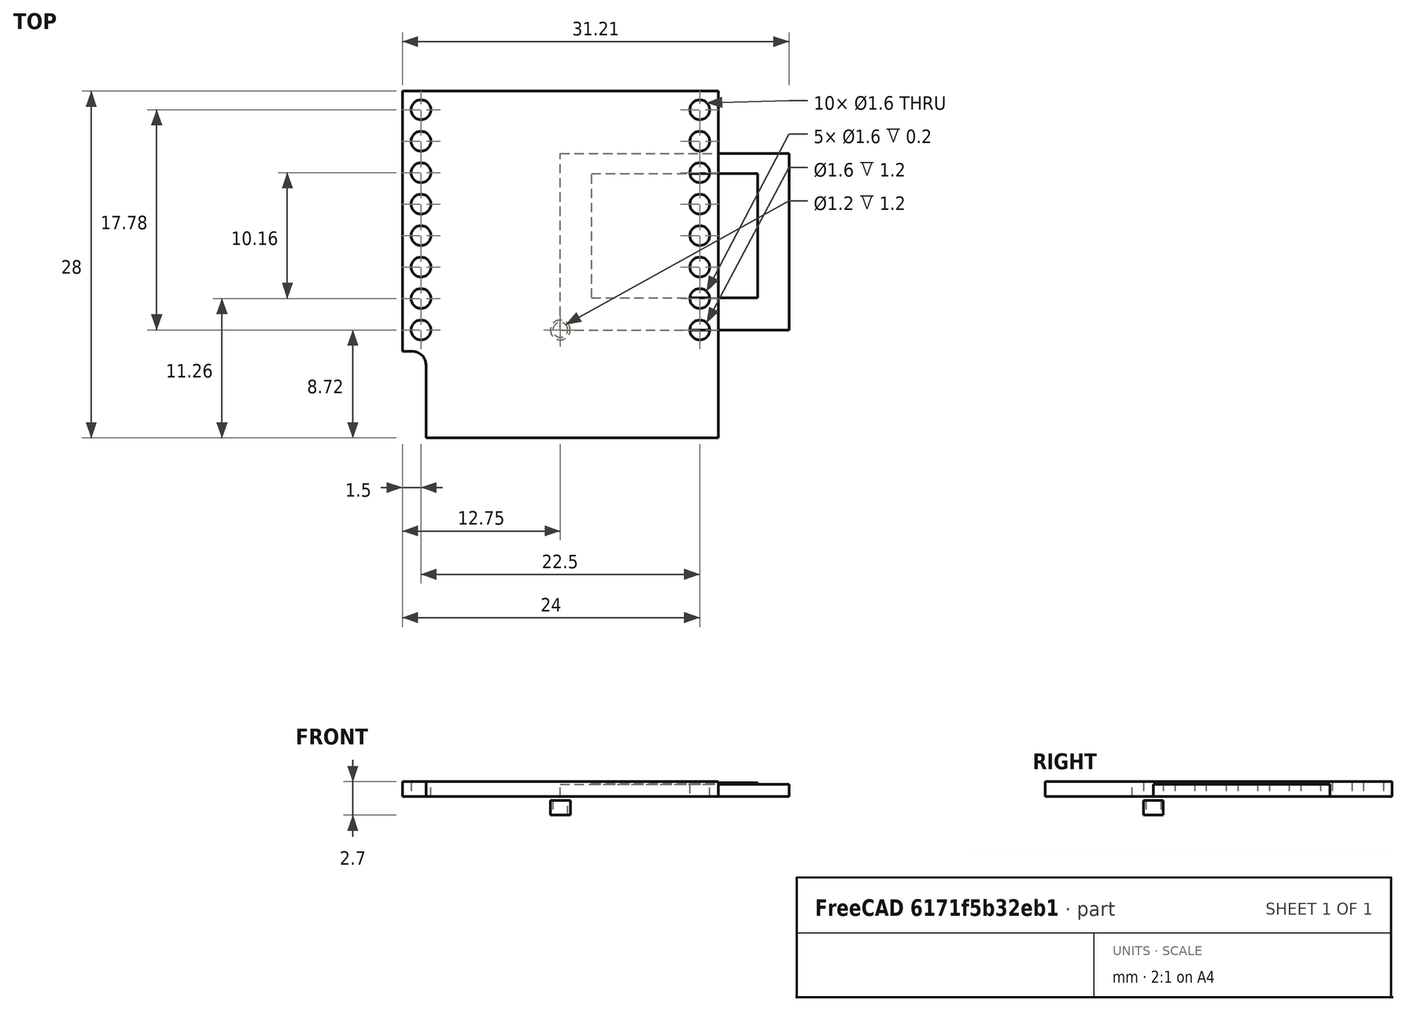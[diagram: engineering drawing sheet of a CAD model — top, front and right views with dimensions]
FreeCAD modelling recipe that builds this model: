
FCSTD DOCUMENT  (FreeCAD 1.0R39109 (Git))
Label: az-oled-066.fcstd
License: All rights reserved
LicenseURL: https://en.wikipedia.org/wiki/All_rights_reserved
objects: App::Link×17, PartDesign::FeatureBase×5, PartDesign::Body×5, Part::Cylinder×2, Part::Box×2, Sketcher::SketchObject×1, Part::Cut×1, App::FeaturePython×1, Assembly::JointGroup×1, Assembly::AssemblyObject×1, PartDesign::Pad×1, Part::Fuse×1, App::DocumentObjectGroup×1
note: 26 computed .brp shape members not serialized (recipe doc carries the construction recipe); baked Part::Feature solids carry a one-line shape summary decoded from their .brp

FEATURE [Sketcher::SketchObject] Sketch
  ArcFitTolerance = 1e-06
  AttachmentSupport = -> [XY_Plane]
  FullyConstrained = true
  MakeInternals = false
  MapMode = 5
  sketch-geometry (26):
    g0: LineSegment StartX=-12.75 StartY=19.28 StartZ=0 EndX=-12.75 EndY=-1.72 EndZ=0
    g1: LineSegment StartX=-10.85 StartY=-8.72 StartZ=0 EndX=12.75 EndY=-8.72 EndZ=0
    g2: LineSegment StartX=12.75 StartY=-8.72 StartZ=0 EndX=12.75 EndY=19.28 EndZ=0
    g3: LineSegment StartX=12.75 StartY=19.28 StartZ=0 EndX=-12.75 EndY=19.28 EndZ=0
    g4: Circle CenterX=-11.25 CenterY=6.02253e-11 CenterZ=0 NormalX=0 NormalY=0 NormalZ=1 AngleXU=0 Radius=0.8
    g5: Circle CenterX=-11.25 CenterY=2.54 CenterZ=0 NormalX=0 NormalY=0 NormalZ=1 AngleXU=0 Radius=0.8
    g6: Circle CenterX=-11.25 CenterY=5.08 CenterZ=0 NormalX=0 NormalY=0 NormalZ=1 AngleXU=0 Radius=0.8
    g7: Circle CenterX=-11.25 CenterY=7.62 CenterZ=0 NormalX=0 NormalY=0 NormalZ=1 AngleXU=0 Radius=0.8
    g8: Circle CenterX=-11.25 CenterY=10.16 CenterZ=0 NormalX=0 NormalY=0 NormalZ=1 AngleXU=0 Radius=0.8
    g9: Circle CenterX=-11.25 CenterY=12.7 CenterZ=0 NormalX=0 NormalY=0 NormalZ=1 AngleXU=0 Radius=0.8
    g10: Circle CenterX=-11.25 CenterY=15.24 CenterZ=0 NormalX=0 NormalY=0 NormalZ=1 AngleXU=0 Radius=0.8
    g11: Circle CenterX=-11.25 CenterY=17.78 CenterZ=0 NormalX=0 NormalY=0 NormalZ=1 AngleXU=0 Radius=0.8
    g12: LineSegment [constr] StartX=5.6891e-12 StartY=19.28 StartZ=0 EndX=5.6891e-12 EndY=-8.72 EndZ=0
    g13: Circle CenterX=11.25 CenterY=6.02253e-11 CenterZ=0 NormalX=0 NormalY=0 NormalZ=1 AngleXU=0 Radius=0.8
    g14: Circle CenterX=11.25 CenterY=2.54 CenterZ=0 NormalX=0 NormalY=0 NormalZ=1 AngleXU=0 Radius=0.8
    g15: Circle CenterX=11.25 CenterY=5.08 CenterZ=0 NormalX=0 NormalY=0 NormalZ=1 AngleXU=0 Radius=0.8
    g16: Circle CenterX=11.25 CenterY=7.62 CenterZ=0 NormalX=0 NormalY=0 NormalZ=1 AngleXU=0 Radius=0.8
    g17: Circle CenterX=11.25 CenterY=10.16 CenterZ=0 NormalX=0 NormalY=0 NormalZ=1 AngleXU=0 Radius=0.8
    g18: Circle CenterX=11.25 CenterY=12.7 CenterZ=0 NormalX=0 NormalY=0 NormalZ=1 AngleXU=0 Radius=0.8
    g19: Circle CenterX=11.25 CenterY=15.24 CenterZ=0 NormalX=0 NormalY=0 NormalZ=1 AngleXU=0 Radius=0.8
    g20: Circle CenterX=11.25 CenterY=17.78 CenterZ=0 NormalX=0 NormalY=0 NormalZ=1 AngleXU=0 Radius=0.8
    g21: LineSegment [constr] StartX=-11.25 StartY=6.02253e-11 StartZ=0 EndX=0 EndY=0 EndZ=0
    g22: LineSegment [constr] StartX=11.25 StartY=6.02253e-11 StartZ=0 EndX=0 EndY=0 EndZ=0
    g23: LineSegment StartX=-12.75 StartY=-1.72 StartZ=0 EndX=-11.95 EndY=-1.72 EndZ=0
    g24: LineSegment StartX=-10.85 StartY=-8.72 StartZ=0 EndX=-10.85 EndY=-2.82 EndZ=0
    g25: ArcOfCircle CenterX=-11.95 CenterY=-2.82 CenterZ=0 NormalX=0 NormalY=0 NormalZ=1 AngleXU=0 Radius=1.1 StartAngle=1e-16 EndAngle=1.5708
  constraints (64):
    c: Coincident(g1,g2)
    c: Vertical(g0)
    c: Vertical(g2)
    c: Horizontal(g3)
    c: Diameter(g4) = 1.6
    c: Equal(g4, g5-g11) x7
    c: DistanceY(g4,g5) = 2.54
    c: DistanceY(g5,g6) = 2.54
    c: DistanceY(g6,g7) = 2.54
    c: DistanceY(g7,g8) = 2.54
    c: DistanceY(g8,g9) = 2.54
    c: DistanceY(g9,g10) = 2.54
    c: DistanceY(g10,g11) = 2.54
    c: Diameter(g13) = 1.6
    c: Equal(g13, g14-g20) x7
    c: Vertical(g13,g14)
    c: Vertical(g14,g15)
    c: Vertical(g15,g16)
    c: Vertical(g16,g17)
    c: Vertical(g17,g18)
    c: Vertical(g18,g19)
    c: Vertical(g19,g20)
    c: Horizontal(g4,g13)
    c: Horizontal(g5,g14)
    c: Horizontal(g6,g15)
    c: Horizontal(g7,g16)
    c: Horizontal(g8,g17)
    c: Horizontal(g9,g18)
    c: Horizontal(g10,g19)
    c: Horizontal(g11,g20)
    c: Coincident(g22,g13)
    c: Coincident(g22,g21)
    c: Equal(g22,g21)
    c: DistanceY(g11,g0) = 1.5
    c: Horizontal(g23)
    c: Vertical(g24)
    c: DistanceY(g24,g23) = 7
    c: Tangent(g25,g24) = -1.5708
    c: Tangent(g25,g23) = 1.5708
    c: Coincident(g1,g24)
    c: Coincident(g0,g23)
    c: PointOnObject(g12,g1)
    c: DistanceY(g1,g2) = 28
    c: DistanceX(g1,g1) = 23.6
    c: DistanceX(g0,g23) = 0.8
    c: PointOnObject(g12,g3)
    c: Perpendicular(g12,g3)
    c: Perpendicular(g2,g1)
    c: Coincident(g3,g2)
    c: Coincident(g0,g3)
    c: DistanceX(g0,g2) = 25.5
    c: DistanceX(g0,g11) = 1.5
    c: PointOnObject(g21,g12)
    c: Vertical(g11,g10)
    c: Vertical(g10,g9)
    c: Vertical(g9,g8)
    c: Vertical(g8,g7)
    c: Vertical(g7,g6)
    c: Vertical(g6,g5)
    c: Vertical(g5,g4)
    c: Coincident(g21,g4)
    c: Perpendicular(g12,g21)
    c: DistanceX(g20,g2) = 1.5
    c: Coincident(g21,g-1)
FEATURE [Part::Cylinder] Cylinder  label="Zylinder"
  Angle = 360
  AttacherType = Attacher::AttachEngine3D
  FirstAngle = 0
  Height = 1.2
  Radius = 0.8
  SecondAngle = 0
FEATURE [Part::Cylinder] Cylinder001  label="Zylinder001"
  Angle = 360
  AttacherType = Attacher::AttachEngine3D
  FirstAngle = 0
  Height = 1.2
  Radius = 0.6
  SecondAngle = 0
FEATURE [Part::Cut] Cut  label="Via-Konstruktion"
  Base = -> Cylinder
  Tool = -> Cylinder001
FEATURE [PartDesign::FeatureBase] Clone
  BaseFeature = -> Cut
  Placement = pos=(0,0,-1.5) rot=(0,0,1;0rad)
  Suppressed = false
FEATURE [PartDesign::Body] Body001  label="Via"
  AllowCompound = false
  Group = -> [Clone]
  Origin = -> Origin001
  Tip = -> Clone
FEATURE [App::Link] Platine  label="Platine001"
  LinkedObject = -> Body002
FEATURE [App::FeaturePython] GroundedJoint  # Assembly grounded joint (typed FeaturePython)
  ObjectToGround = -> Platine
FEATURE [Assembly::JointGroup] Joints
  Group = -> [GroundedJoint]
FEATURE [App::Link] Via  label="Via001"
  LinkPlacement = pos=(15.305,14.26,-1e-16) rot=(0,1,0;4.71239rad)
  LinkedObject = -> Body001
  Placement = pos=(15.305,14.26,-1e-16) rot=(0,1,0;4.71239rad)
FEATURE [App::Link] Via001  label="Via002"
  LinkPlacement = pos=(-11.25,2.54,0.3) rot=(0,0,1;3.14159rad)
  LinkedObject = -> Body001
  Placement = pos=(-11.25,2.54,0.3) rot=(0,0,1;3.14159rad)
FEATURE [App::Link] Via002  label="Via003"
  LinkPlacement = pos=(11.25,17.48,0) rot=(-0.57735,0.57735,-0.57735;4.18879rad)
  LinkedObject = -> Body001
  Placement = pos=(11.25,17.48,0) rot=(-0.57735,0.57735,-0.57735;4.18879rad)
FEATURE [App::Link] Via003  label="Via004"
  LinkPlacement = pos=(11.55,15.24,-1e-16) rot=(0,1,0;1.5708rad)
  LinkedObject = -> Body001
  Placement = pos=(11.55,15.24,-1e-16) rot=(0,1,0;1.5708rad)
FEATURE [App::Link] Via004  label="Via005"
  LinkPlacement = pos=(-11.25,6.02253e-11,0.3) rot=(0,0,1;0rad)
  LinkedObject = -> Body001
  Placement = pos=(-11.25,6.02253e-11,0.3) rot=(0,0,1;0rad)
FEATURE [App::Link] Via005  label="Via006"
  LinkPlacement = pos=(-11.55,17.78,-1e-16) rot=(0.584443,-0.562897,-0.584443;2.11621rad)
  LinkedObject = -> Body001
  Placement = pos=(-11.55,17.78,-1e-16) rot=(0.584443,-0.562897,-0.584443;2.11621rad)
FEATURE [App::Link] Via006  label="Via007"
  LinkPlacement = pos=(-11.25,5.08,0.3) rot=(0,0,1;0rad)
  LinkedObject = -> Body001
  Placement = pos=(-11.25,5.08,0.3) rot=(0,0,1;0rad)
FEATURE [App::Link] Via007  label="Via008"
  LinkPlacement = pos=(11.25,7.62,0.3) rot=(0,0,1;0rad)
  LinkedObject = -> Body001
  Placement = pos=(11.25,7.62,0.3) rot=(0,0,1;0rad)
FEATURE [App::Link] Via008  label="Via009"
  LinkPlacement = pos=(-11.25,15.24,-0.3) rot=(0,1,0;3.14159rad)
  LinkedObject = -> Body001
  Placement = pos=(-11.25,15.24,-0.3) rot=(0,1,0;3.14159rad)
FEATURE [App::Link] Via009  label="Via010"
  LinkPlacement = pos=(12.75,16.47,0) rot=(0.57735,-0.57735,0.57735;2.0944rad)
  LinkedObject = -> Body001
  Placement = pos=(12.75,16.47,0) rot=(0.57735,-0.57735,0.57735;2.0944rad)
FEATURE [App::Link] Via010  label="Via011"
  LinkPlacement = pos=(-11.25,7.62,0.3) rot=(0,0,1;0rad)
  LinkedObject = -> Body001
  Placement = pos=(-11.25,7.62,0.3) rot=(0,0,1;0rad)
FEATURE [App::Link] Via011  label="Via012"
  LinkPlacement = pos=(-11.25,10.16,0.3) rot=(0,0,1;0rad)
  LinkedObject = -> Body001
  Placement = pos=(-11.25,10.16,0.3) rot=(0,0,1;0rad)
FEATURE [App::Link] Via012  label="Via013"
  LinkPlacement = pos=(11.55,6.02253e-11,0) rot=(-0.561257,0.608261,-0.561257;2.04865rad)
  LinkedObject = -> Body001
  Placement = pos=(11.55,6.02253e-11,0) rot=(-0.561257,0.608261,-0.561257;2.04865rad)
FEATURE [App::Link] Via013  label="Via014"
  LinkPlacement = pos=(-11.25,12.7,0.3) rot=(0,0,1;0rad)
  LinkedObject = -> Body001
  Placement = pos=(-11.25,12.7,0.3) rot=(0,0,1;0rad)
FEATURE [App::Link] Via014  label="Via015"
  LinkPlacement = pos=(12.75,-4.36,0.3) rot=(0,0,1;0rad)
  LinkedObject = -> Body001
  Placement = pos=(12.75,-4.36,0.3) rot=(0,0,1;0rad)
FEATURE [App::Link] Via015  label="Via016"
  LinkPlacement = pos=(0.65,-8.72,-1e-16) rot=(0,1,0;4.71239rad)
  LinkedObject = -> Body001
  Placement = pos=(0.65,-8.72,-1e-16) rot=(0,1,0;4.71239rad)
FEATURE [Assembly::AssemblyObject] Assembly
  Group = -> [Joints,Platine,GroundedJoint,Via,Via001,Via002,Via003,Via004,Via005,Via006,Via007,Via008,Via009,Via010,Via011,Via012,Via013,Via014,Via015]
  Origin = -> Origin004
  Type = Assembly
FEATURE [Part::Box] Box001  label="Display-Kontruktion"
  AttacherType = Attacher::AttachEngine3D
  Height = 1
  Length = 18.46
  Width = 14.26
FEATURE [Part::Box] Box  label="DisplayActive-Kontruktion"
  AttacherType = Attacher::AttachEngine3D
  Height = 0.1
  Length = 13.42
  Placement = pos=(2.52,2.6,1) rot=(0,0,1;0rad)
  Width = 10.02
FEATURE [PartDesign::FeatureBase] BaseFeature
  BaseFeature = -> Box001
  Suppressed = false
FEATURE [PartDesign::Pad] Pad  label="Pad Platine"
  BaseFeature = -> BaseFeature
  Direction = (0,0,1)
  Length = 1.2
  Length2 = 10
  Profile = -> Sketch
  ReferenceAxis = -> Sketch [N_Axis]
  Suppressed = false
  Type = 0
FEATURE [PartDesign::Body] Body  label="Platine-Konstruktion"
  AllowCompound = false
  BaseFeature = -> Box001
  Group = -> [BaseFeature,Sketch,Pad]
  Origin = -> Origin
  Tip = -> Pad
FEATURE [PartDesign::FeatureBase] Clone001
  BaseFeature = -> Body
  Suppressed = false
FEATURE [PartDesign::Body] Body002  label="Platine"
  AllowCompound = false
  Group = -> [Clone001]
  Origin = -> Origin002
  Tip = -> Clone001
FEATURE [PartDesign::FeatureBase] Clone002
  BaseFeature = -> Box
  Placement = pos=(2.52,2.6,1) rot=(0,0,1;0rad)
  Suppressed = false
FEATURE [PartDesign::Body] Body003  label="DispActive"
  AllowCompound = false
  Group = -> [Clone002]
  Origin = -> Origin005
  Tip = -> Clone002
FEATURE [PartDesign::FeatureBase] Clone003
  BaseFeature = -> Box001
  Suppressed = false
FEATURE [PartDesign::Body] Body004  label="Dispcarrier"
  AllowCompound = false
  Group = -> [Clone003]
  Origin = -> Origin006
  Tip = -> Clone003
FEATURE [Part::Fuse] Fusion  label="Display"
  Base = -> Body003
  Tool = -> Body004
FEATURE [App::DocumentObjectGroup] Group  label="Gruppe"
  Group = -> [Body002,Body001,Fusion]
